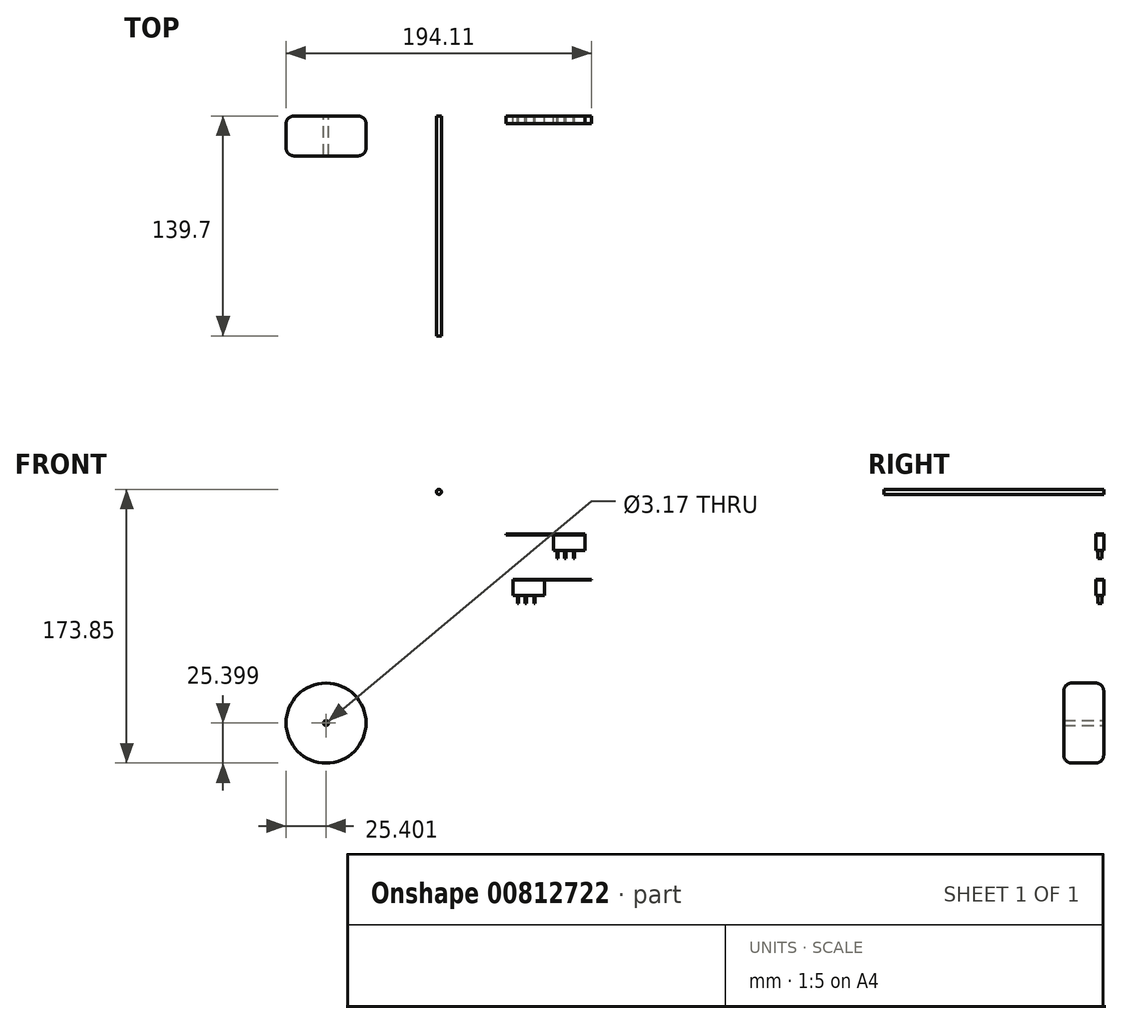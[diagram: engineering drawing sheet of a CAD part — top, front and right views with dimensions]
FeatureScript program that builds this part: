
annotation { "Feature Type Name" : "Feature", "Feature Type Description" : "" }
export const myFeature = defineFeature(function(context is Context, id is Id, definition is map)
    precondition{}
    {
        {
            var Q0;
            Q0=qCreatedBy(makeId("Front.planeOp"),FACE);
            var sketch = newSketch(context, id + "F0", { "sketchPlane" : qUnion([Q0])});
            skLineSegment(sketch, "E0.bottom", {"start": v(-13.56, -14.31) * mm, "end": v(6.44, -14.31) * mm});
            skLineSegment(sketch, "E0.top", {"start": v(-13.56, -24.31) * mm, "end": v(6.44, -24.31) * mm});
            skLineSegment(sketch, "E0.left", {"start": v(-13.56, -14.31) * mm, "end": v(-13.56, -24.31) * mm});
            skLineSegment(sketch, "E0.right", {"start": v(6.44, -14.31) * mm, "end": v(6.44, -24.31) * mm});
            skLineSegment(sketch, "E1.bottom", {"start": v(12.15, 14.3) * mm, "end": v(32.15, 14.3) * mm});
            skLineSegment(sketch, "E1.top", {"start": v(12.15, 4.3) * mm, "end": v(32.15, 4.3) * mm});
            skLineSegment(sketch, "E1.left", {"start": v(12.15, 14.3) * mm, "end": v(12.15, 4.3) * mm});
            skLineSegment(sketch, "E1.right", {"start": v(32.15, 14.3) * mm, "end": v(32.15, 4.3) * mm});
            skSolve(sketch);
        }
        {
            var Q0;
            Q0=makeQuery(id+"F0.imprint","IMPRINT",FACE,{"disambiguationData":[TD([[makeQuery(id+"F0.imprint","IMPRINT",EDGE,{"derivedFrom":sQuery(id+"F0.wireOp",EDGE,"E0.bottom")}),-1.0]])]});
            var Q1;
            Q1=makeQuery(id+"F0.imprint","IMPRINT",FACE,{"disambiguationData":[TD([[makeQuery(id+"F0.imprint","IMPRINT",EDGE,{"derivedFrom":sQuery(id+"F0.wireOp",EDGE,"E1.bottom")}),-1.0]])]});
            extrude(context, id + "F1", {"entities" : qUnion([Q0, Q1]), "depth" : 5 * mm, "offsetDistance" : 25.4 * mm});
        }
        {
            var Q0;
            Q0=makeQuery(id+"F1.opExtrude","SWEPT_FACE",FACE,{"disambiguationData":[OSD([sQuery(id+"F0.wireOp",EDGE,"E1.bottom")])]});
            var sketch = newSketch(context, id + "F2", { "sketchPlane" : qUnion([Q0])});
            skLineSegment(sketch, "E2", {"start": v(32.15, -5) * mm, "end": v(-17.85, -5) * mm});
            skLineSegment(sketch, "E3", {"start": v(-17.85, -5) * mm, "end": v(-17.85, 0) * mm});
            skLineSegment(sketch, "E4", {"start": v(-17.85, 0) * mm, "end": v(32.15, 0) * mm});
            skLineSegment(sketch, "E5", {"start": v(32.15, 0) * mm, "end": v(32.15, -5) * mm});
            skSolve(sketch);
        }
        {
            var Q0;
            Q0=makeQuery(id+"F1.opExtrude","SWEPT_FACE",FACE,{"disambiguationData":[OSD([sQuery(id+"F0.wireOp",EDGE,"E0.bottom")])]});
            var sketch = newSketch(context, id + "F3", { "sketchPlane" : qUnion([Q0])});
            skLineSegment(sketch, "E6", {"start": v(36.44, -5) * mm, "end": v(-13.56, -5) * mm});
            skLineSegment(sketch, "E7", {"start": v(-13.56, -5) * mm, "end": v(-13.56, 0) * mm});
            skLineSegment(sketch, "E8", {"start": v(-13.56, 0) * mm, "end": v(36.44, 0) * mm});
            skLineSegment(sketch, "E9", {"start": v(36.44, 0) * mm, "end": v(36.44, -5) * mm});
            skSolve(sketch);
        }
        {
            var Q0;
            {var subQ2=sQuery(id+"F2.wireOp",EDGE,"E5");Q0=makeQuery(id+"F2.imprint","IMPRINT",FACE,{"disambiguationData":[TD([[makeQuery(id+"F2.imprint","IMPRINT",EDGE,{"derivedFrom":subQ2}),1.0]])]});}
            var Q1;
            {var subQ2=sQuery(id+"F2.wireOp",EDGE,"E3");Q1=makeQuery(id+"F2.imprint","IMPRINT",FACE,{"disambiguationData":[TD([[makeQuery(id+"F2.imprint","IMPRINT",EDGE,{"derivedFrom":subQ2}),-1.0]])]});}
            var Q2;
            {var subQ2=sQuery(id+"F3.wireOp",EDGE,"E9");Q2=makeQuery(id+"F3.imprint","IMPRINT",FACE,{"disambiguationData":[TD([[makeQuery(id+"F3.imprint","IMPRINT",EDGE,{"derivedFrom":subQ2}),-1.0]])]});}
            var Q3;
            {var subQ0=sQuery(id+"F3.wireOp",EDGE,"E7");Q3=makeQuery(id+"F3.imprint","IMPRINT",FACE,{"disambiguationData":[TD([[makeQuery(id+"F3.imprint","IMPRINT",EDGE,{"derivedFrom":subQ0}),-1.0]])]});}
            extrude(context, id + "F4", {"entities" : qUnion([Q0, Q1, Q2, Q3]), "depth" : 0.4 * mm, "offsetDistance" : 25.4 * mm});
        }
        {
            var Q0;
            Q0=makeQuery(id+"F1.opExtrude","SWEPT_FACE",FACE,{"disambiguationData":[OSD([sQuery(id+"F0.wireOp",EDGE,"E1.top")])]});
            var sketch = newSketch(context, id + "F5", { "sketchPlane" : qUnion([Q0])});
            skLineSegment(sketch, "E10.bottom", {"start": v(14.34, 3.67) * mm, "end": v(15.07, 3.67) * mm});
            skLineSegment(sketch, "E10.top", {"start": v(14.34, 1.13) * mm, "end": v(15.07, 1.13) * mm});
            skLineSegment(sketch, "E10.left", {"start": v(14.34, 3.67) * mm, "end": v(14.34, 1.13) * mm});
            skLineSegment(sketch, "E10.right", {"start": v(15.07, 3.67) * mm, "end": v(15.07, 1.13) * mm});
            skLineSegment(sketch, "E11.bottom", {"start": v(19.02, 3.67) * mm, "end": v(19.96, 3.67) * mm});
            skLineSegment(sketch, "E11.top", {"start": v(19.02, 1.13) * mm, "end": v(19.96, 1.13) * mm});
            skLineSegment(sketch, "E11.left", {"start": v(19.02, 3.67) * mm, "end": v(19.02, 1.13) * mm});
            skLineSegment(sketch, "E11.right", {"start": v(19.96, 3.67) * mm, "end": v(19.96, 1.13) * mm});
            skLineSegment(sketch, "E12.bottom", {"start": v(24.85, 3.67) * mm, "end": v(25.49, 3.67) * mm});
            skLineSegment(sketch, "E12.top", {"start": v(24.85, 1.13) * mm, "end": v(25.49, 1.13) * mm});
            skLineSegment(sketch, "E12.left", {"start": v(24.85, 3.67) * mm, "end": v(24.85, 1.13) * mm});
            skLineSegment(sketch, "E12.right", {"start": v(25.49, 3.67) * mm, "end": v(25.49, 1.13) * mm});
            skSolve(sketch);
        }
        {
            var Q0;
            Q0=makeQuery(id+"F1.opExtrude","SWEPT_FACE",FACE,{"disambiguationData":[OSD([sQuery(id+"F0.wireOp",EDGE,"E0.top")])]});
            var sketch = newSketch(context, id + "F6", { "sketchPlane" : qUnion([Q0])});
            skLineSegment(sketch, "E13.bottom", {"start": v(-10.69, 3.72) * mm, "end": v(-9.96, 3.72) * mm});
            skLineSegment(sketch, "E13.top", {"start": v(-10.69, 1.19) * mm, "end": v(-9.96, 1.19) * mm});
            skLineSegment(sketch, "E13.left", {"start": v(-10.69, 3.72) * mm, "end": v(-10.69, 1.19) * mm});
            skLineSegment(sketch, "E13.right", {"start": v(-9.96, 3.72) * mm, "end": v(-9.96, 1.19) * mm});
            skLineSegment(sketch, "E14.bottom", {"start": v(-6, 3.72) * mm, "end": v(-5.07, 3.72) * mm});
            skLineSegment(sketch, "E14.top", {"start": v(-6, 1.19) * mm, "end": v(-5.07, 1.19) * mm});
            skLineSegment(sketch, "E14.left", {"start": v(-6, 3.72) * mm, "end": v(-6, 1.19) * mm});
            skLineSegment(sketch, "E14.right", {"start": v(-5.07, 3.72) * mm, "end": v(-5.07, 1.19) * mm});
            skLineSegment(sketch, "E15.bottom", {"start": v(-0.18, 3.72) * mm, "end": v(0.46, 3.72) * mm});
            skLineSegment(sketch, "E15.top", {"start": v(-0.18, 1.19) * mm, "end": v(0.46, 1.19) * mm});
            skLineSegment(sketch, "E15.left", {"start": v(-0.18, 3.72) * mm, "end": v(-0.18, 1.19) * mm});
            skLineSegment(sketch, "E15.right", {"start": v(0.46, 3.72) * mm, "end": v(0.46, 1.19) * mm});
            skSolve(sketch);
        }
        {
            var Q0;
            Q0 = qSketchRegion(id + "F5", true);
            var Q1;
            Q1 = qSketchRegion(id + "F6", true);
            extrude(context, id + "F7", {"entities" : qUnion([Q0, Q1]), "operationType" : NewBodyOperationType.ADD, "depth" : 5 * mm, "offsetDistance" : 25.4 * mm});
        }
        {
            var Q0;
            Q0=qCreatedBy(makeId("Front.planeOp"),FACE);
            var sketch = newSketch(context, id + "F8", { "sketchPlane" : qUnion([Q0])});
            skCircle(sketch, "E16", {"center": v(-60.62, 41.62) * mm, "radius": 1.59 * mm});
            skSolve(sketch);
        }
        {
            var Q0;
            Q0 = qSketchRegion(id + "F8", true);
            extrude(context, id + "F9", {"entities" : qUnion([Q0]), "depth" : 139.7 * mm, "offsetDistance" : 25.4 * mm});
        }
        {
            var Q0;
            Q0=qCreatedBy(makeId("Front.planeOp"),FACE);
            var sketch = newSketch(context, id + "F10", { "sketchPlane" : qUnion([Q0])});
            skCircle(sketch, "E17", {"center": v(-132.27, -105.25) * mm, "radius": 25.4 * mm});
            skSolve(sketch);
        }
        {
            var Q0;
            Q0 = qSketchRegion(id + "F10", true);
            var Q1;
            Q1=makeQuery(id+"F10.imprint","IMPRINT",FACE,{"disambiguationData":[TD([[makeQuery(id+"F10.imprint","IMPRINT",EDGE,{"derivedFrom":sQuery(id+"F10.wireOp",EDGE,"E17")}),1.0]])]});
            extrude(context, id + "F11", {"entities" : qUnion([Q0, Q1]), "depth" : 25.4 * mm, "offsetDistance" : 25.4 * mm});
        }
        {
            var Q0;
            Q0=sQuery(id+"F10.wireOp",VERTEX,"E17.center");
            var Q1;
            Q1=makeQuery(id+"F11.opExtrude","SWEPT_BODY",BODY,{"disambiguationData":[OSD([sQuery(id+"F10.wireOp",EDGE,"E17")])]});
            hole(context, id + "F12", {"style" : HoleStyle.SIMPLE, "endStyle" : HoleEndStyle.THROUGH, "oppositeDirection" : true, "holeDiameter" : 3.17 * mm, "majorDiameter" : 6.35 * mm, "isTappedThrough" : true, "tappedDepth" : 12.7 * mm, "tapClearance" : 3, "locations" : qUnion([Q0]), "scope" : qUnion([Q1])});
        }
        {
            var Q0;
            Q0=makeQuery(id+"F11.opExtrude","CAP_EDGE",EDGE,{"disambiguationData":[OSD([sQuery(id+"F10.wireOp",EDGE,"E17")])],"isStart":false});
            var Q1;
            Q1=makeQuery(id+"F11.opExtrude","CAP_EDGE",EDGE,{"disambiguationData":[OSD([sQuery(id+"F10.wireOp",EDGE,"E17")])],"isStart":true});
            fillet(context, id + "F13", {"entities" : qUnion([Q0, Q1]), "radius" : 5.08 * mm, "tangentPropagation" : true, "allowEdgeOverflow" : false});
        }
    });
